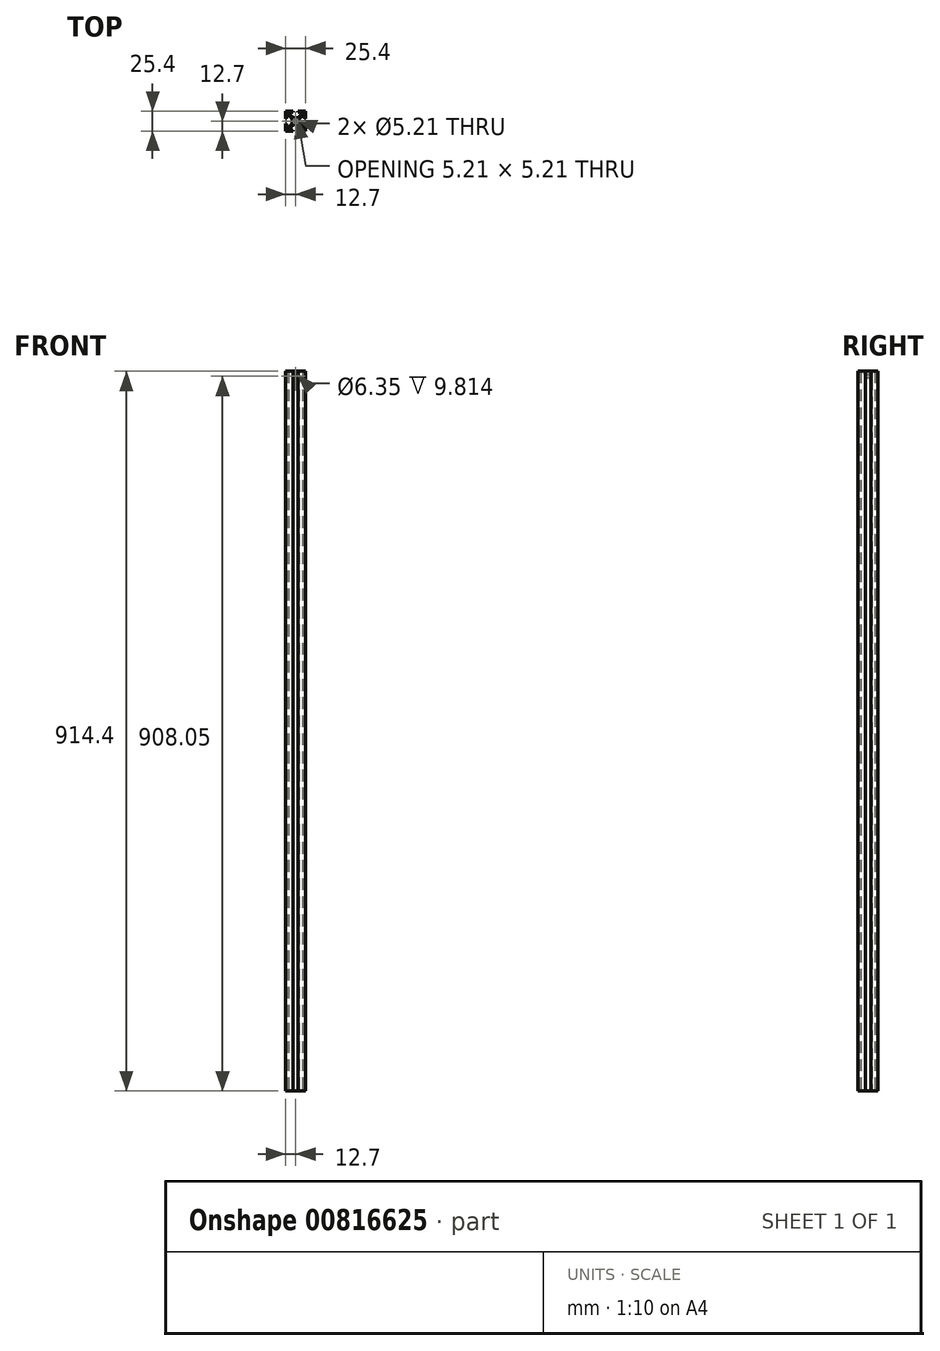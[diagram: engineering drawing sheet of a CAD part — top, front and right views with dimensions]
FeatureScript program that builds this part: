
annotation { "Feature Type Name" : "Feature", "Feature Type Description" : "" }
export const myFeature = defineFeature(function(context is Context, id is Id, definition is map)
    precondition{}
    {
        {
            var Q0;
            Q0=qCreatedBy(makeId("Top.planeOp"),FACE);
            var sketch = newSketch(context, id + "F0", { "sketchPlane" : qUnion([Q0])});
            skLineSegment(sketch, "E0.bottom", {"start": v(12.7, 12.7) * mm, "end": v(-12.7, 12.7) * mm, "construction": true});
            skLineSegment(sketch, "E0.top", {"start": v(12.7, -12.7) * mm, "end": v(-12.7, -12.7) * mm, "construction": true});
            skLineSegment(sketch, "E0.left", {"start": v(12.7, 12.7) * mm, "end": v(12.7, -12.7) * mm, "construction": true});
            skLineSegment(sketch, "E0.right", {"start": v(-12.7, 12.7) * mm, "end": v(-12.7, -12.7) * mm, "construction": true});
            skPoint(sketch, "E0.middle", {"position": v(0, 0) * mm});
            skCircle(sketch, "E1", {"center": v(0, 0) * mm, "radius": 2.6 * mm});
            skLineSegment(sketch, "E2", {"start": v(-12.7, -12.7) * mm, "end": v(12.7, 12.7) * mm, "construction": true});
            skLineSegment(sketch, "E3", {"start": v(-12.7, 12.7) * mm, "end": v(12.7, -12.7) * mm, "construction": true});
            skLineSegment(sketch, "E4", {"start": v(5.43, 3.86) * mm, "end": v(10.24, 8.68) * mm});
            skLineSegment(sketch, "E5", {"start": v(4.5, 1.62) * mm, "end": v(4.5, 0) * mm});
            skLineSegment(sketch, "E6", {"start": v(11.6, 8.12) * mm, "end": v(11.6, 3.24) * mm});
            skLineSegment(sketch, "E7", {"start": v(11.6, 3.24) * mm, "end": v(12.7, 3.24) * mm});
            skPoint(sketch, "E8.visualSharp", {"position": v(4.5, 2.93) * mm});
            skArc(sketch, "E8.filletArc", {"start": v(5.43, 3.86) * mm, "mid": v(4.74, 2.83) * mm, "end": v(4.5, 1.62) * mm});
            skPoint(sketch, "E9.visualSharp", {"position": v(11.6, 10.03) * mm});
            skArc(sketch, "E9.filletArc", {"start": v(11.6, 8.12) * mm, "mid": v(11.1, 8.85) * mm, "end": v(10.24, 8.68) * mm});
            skLineSegment(sketch, "E10.MirrorCS", {"start": v(4.5, -1.62) * mm, "end": v(4.5, 0) * mm});
            skArc(sketch, "E11.MirrorCS", {"start": v(11.6, -8.12) * mm, "mid": v(11.1, -8.85) * mm, "end": v(10.24, -8.68) * mm});
            skLineSegment(sketch, "E12.MirrorCS", {"start": v(11.6, -3.24) * mm, "end": v(12.7, -3.24) * mm});
            skArc(sketch, "E13.MirrorCS", {"start": v(5.43, -3.86) * mm, "mid": v(4.74, -2.83) * mm, "end": v(4.5, -1.62) * mm});
            skLineSegment(sketch, "E14.MirrorCS", {"start": v(11.6, -8.12) * mm, "end": v(11.6, -3.24) * mm});
            skLineSegment(sketch, "E15.MirrorCS", {"start": v(5.43, -3.86) * mm, "end": v(10.24, -8.68) * mm});
            skPoint(sketch, "E16.MirrorP", {"position": v(11.6, -10.03) * mm});
            skPoint(sketch, "E17.MirrorP", {"position": v(4.5, -2.93) * mm});
            skLineSegment(sketch, "E18.MirrorCS", {"start": v(-1.62, 4.5) * mm, "end": v(0, 4.5) * mm});
            skLineSegment(sketch, "E19.MirrorCS", {"start": v(1.62, 4.5) * mm, "end": v(0, 4.5) * mm});
            skArc(sketch, "E20.MirrorCS", {"start": v(3.86, 5.43) * mm, "mid": v(2.83, 4.74) * mm, "end": v(1.62, 4.5) * mm});
            skLineSegment(sketch, "E21.MirrorCS", {"start": v(3.24, 11.6) * mm, "end": v(3.24, 12.7) * mm});
            skLineSegment(sketch, "E22.MirrorCS", {"start": v(-3.24, 11.6) * mm, "end": v(-3.24, 12.7) * mm});
            skArc(sketch, "E23.MirrorCS", {"start": v(-3.86, 5.43) * mm, "mid": v(-2.83, 4.74) * mm, "end": v(-1.62, 4.5) * mm});
            skArc(sketch, "E24.MirrorCS", {"start": v(8.12, 11.6) * mm, "mid": v(8.85, 11.1) * mm, "end": v(8.68, 10.24) * mm});
            skPoint(sketch, "E25.MirrorP", {"position": v(2.93, 4.5) * mm});
            skLineSegment(sketch, "E26.MirrorCS", {"start": v(-8.12, 11.6) * mm, "end": v(-3.24, 11.6) * mm});
            skPoint(sketch, "E27.MirrorP", {"position": v(-10.03, 11.6) * mm});
            skPoint(sketch, "E28.MirrorP", {"position": v(10.03, 11.6) * mm});
            skPoint(sketch, "E29.MirrorP", {"position": v(-2.93, 4.5) * mm});
            skArc(sketch, "E30.MirrorCS", {"start": v(-8.12, 11.6) * mm, "mid": v(-8.85, 11.1) * mm, "end": v(-8.68, 10.24) * mm});
            skLineSegment(sketch, "E31.MirrorCS", {"start": v(8.12, 11.6) * mm, "end": v(3.24, 11.6) * mm});
            skLineSegment(sketch, "E32.MirrorCS", {"start": v(3.86, 5.43) * mm, "end": v(8.68, 10.24) * mm});
            skLineSegment(sketch, "E33.MirrorCS", {"start": v(-3.86, 5.43) * mm, "end": v(-8.68, 10.24) * mm});
            skLineSegment(sketch, "E34.MirrorCS", {"start": v(-11.6, -3.24) * mm, "end": v(-12.7, -3.24) * mm});
            skLineSegment(sketch, "E35.MirrorCS", {"start": v(-11.6, 3.24) * mm, "end": v(-12.7, 3.24) * mm});
            skArc(sketch, "E36.MirrorCS", {"start": v(-5.43, 3.86) * mm, "mid": v(-4.74, 2.83) * mm, "end": v(-4.5, 1.62) * mm});
            skArc(sketch, "E37.MirrorCS", {"start": v(-5.43, -3.86) * mm, "mid": v(-4.74, -2.83) * mm, "end": v(-4.5, -1.62) * mm});
            skLineSegment(sketch, "E38.MirrorCS", {"start": v(-4.5, -1.62) * mm, "end": v(-4.5, 0) * mm});
            skLineSegment(sketch, "E39.MirrorCS", {"start": v(-11.6, -8.12) * mm, "end": v(-11.6, -3.24) * mm});
            skPoint(sketch, "E40.MirrorP", {"position": v(-4.5, 2.93) * mm});
            skPoint(sketch, "E41.MirrorP", {"position": v(-4.5, -2.93) * mm});
            skArc(sketch, "E42.MirrorCS", {"start": v(-11.6, -8.12) * mm, "mid": v(-11.1, -8.85) * mm, "end": v(-10.24, -8.68) * mm});
            skArc(sketch, "E43.MirrorCS", {"start": v(-11.6, 8.12) * mm, "mid": v(-11.1, 8.85) * mm, "end": v(-10.24, 8.68) * mm});
            skLineSegment(sketch, "E44.MirrorCS", {"start": v(-4.5, 1.62) * mm, "end": v(-4.5, 0) * mm});
            skPoint(sketch, "E45.MirrorP", {"position": v(-11.6, 10.03) * mm});
            skLineSegment(sketch, "E46.MirrorCS", {"start": v(-5.43, -3.86) * mm, "end": v(-10.24, -8.68) * mm});
            skLineSegment(sketch, "E47.MirrorCS", {"start": v(-11.6, 8.12) * mm, "end": v(-11.6, 3.24) * mm});
            skLineSegment(sketch, "E48.MirrorCS", {"start": v(-5.43, 3.86) * mm, "end": v(-10.24, 8.68) * mm});
            skLineSegment(sketch, "E49.MirrorCS", {"start": v(-3.24, -11.6) * mm, "end": v(-3.24, -12.7) * mm});
            skLineSegment(sketch, "E50.MirrorCS", {"start": v(3.24, -11.6) * mm, "end": v(3.24, -12.7) * mm});
            skArc(sketch, "E51.MirrorCS", {"start": v(8.12, -11.6) * mm, "mid": v(8.85, -11.1) * mm, "end": v(8.68, -10.24) * mm});
            skLineSegment(sketch, "E52.MirrorCS", {"start": v(-8.12, -11.6) * mm, "end": v(-3.24, -11.6) * mm});
            skLineSegment(sketch, "E53.MirrorCS", {"start": v(1.62, -4.5) * mm, "end": v(0, -4.5) * mm});
            skArc(sketch, "E54.MirrorCS", {"start": v(-3.86, -5.43) * mm, "mid": v(-2.83, -4.74) * mm, "end": v(-1.62, -4.5) * mm});
            skLineSegment(sketch, "E55.MirrorCS", {"start": v(-1.62, -4.5) * mm, "end": v(0, -4.5) * mm});
            skArc(sketch, "E56.MirrorCS", {"start": v(3.86, -5.43) * mm, "mid": v(2.83, -4.74) * mm, "end": v(1.62, -4.5) * mm});
            skPoint(sketch, "E57.MirrorP", {"position": v(10.03, -11.6) * mm});
            skArc(sketch, "E58.MirrorCS", {"start": v(-8.12, -11.6) * mm, "mid": v(-8.85, -11.1) * mm, "end": v(-8.68, -10.24) * mm});
            skLineSegment(sketch, "E59.MirrorCS", {"start": v(-3.86, -5.43) * mm, "end": v(-8.68, -10.24) * mm});
            skLineSegment(sketch, "E60.MirrorCS", {"start": v(8.12, -11.6) * mm, "end": v(3.24, -11.6) * mm});
            skLineSegment(sketch, "E61.MirrorCS", {"start": v(3.86, -5.43) * mm, "end": v(8.68, -10.24) * mm});
            skLineSegment(sketch, "E62", {"start": v(3.24, 12.7) * mm, "end": v(12.7, 12.7) * mm});
            skLineSegment(sketch, "E63", {"start": v(12.7, 3.24) * mm, "end": v(12.7, 12.7) * mm});
            skLineSegment(sketch, "E64", {"start": v(12.7, -3.24) * mm, "end": v(12.7, -12.7) * mm});
            skLineSegment(sketch, "E65", {"start": v(12.7, -12.7) * mm, "end": v(3.24, -12.7) * mm});
            skLineSegment(sketch, "E66", {"start": v(-3.24, -12.7) * mm, "end": v(-12.7, -12.7) * mm});
            skLineSegment(sketch, "E67", {"start": v(-12.7, -12.7) * mm, "end": v(-12.7, -3.24) * mm});
            skLineSegment(sketch, "E68", {"start": v(-12.7, 3.24) * mm, "end": v(-12.7, 12.7) * mm});
            skLineSegment(sketch, "E69", {"start": v(-12.7, 12.7) * mm, "end": v(-3.24, 12.7) * mm});
            skSolve(sketch);
        }
        {
            var Q0;
            Q0 = qSketchRegion(id + "F0", true);
            extrude(context, id + "F1", {"entities" : qUnion([Q0]), "endBound" : BoundingType.SYMMETRIC, "depth" : 914.4 * mm, "offsetDistance" : 25.4 * mm});
        }
        {
            var Q0;
            Q0=qCreatedBy(makeId("Front.planeOp"),FACE);
            var sketch = newSketch(context, id + "F2", { "sketchPlane" : qUnion([Q0])});
            skCircle(sketch, "E70", {"center": v(0, 450.85) * mm, "radius": 3.18 * mm});
            skSolve(sketch);
        }
        {
            var Q0;
            Q0 = qSketchRegion(id + "F2", true);
            extrude(context, id + "F3", {"entities" : qUnion([Q0]), "operationType" : NewBodyOperationType.REMOVE, "endBound" : BoundingType.SYMMETRIC, "oppositeDirection" : true, "depth" : 50.8 * mm, "offsetDistance" : 25.4 * mm});
        }
    });
